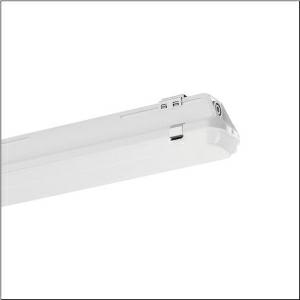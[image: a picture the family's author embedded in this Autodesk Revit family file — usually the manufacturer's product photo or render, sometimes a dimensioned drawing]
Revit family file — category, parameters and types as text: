
# Revit family: monsun_r__21_51fb207l440k005_b217
name_source: partatom
category: Lighting Fixtures
units: mm (PartAtom-declared; Revit-internal decimal feet)

## family parameters
Cut with Voids When Loaded = No
Host = Face
Light Source = No
Part Type = Normal
Room Calculation Point = No
Round Connector Dimension = Use Diameter
Shared = No

## types (1)
- Monsun® 21 (1 x LED, 4330 lm, 27.2 W, 4000K)
    Apparent Load = 27 VA
    CIE Flux Codes = 45 75 93 94 100
    Color Rendering = 80
    Color Temperature = 4000K
    Default Elevation = 1800 mm
    Description = Monsun® 21, damp-proof luminaire, chain hanger, primary optical cover: enclosure, of PC, light emission: direct distribution, primary light characteristic: symmetric, installation type: vertical mounting, horizontal mounting, surface-mounted, suspended mounting, LED, rated luminous flux: 4.330lm, luminous efficacy: 159lm/W, light colour: 840, colour temperature: 4000K, control gear: ON/OFF, with terminal, 3-pole, max. 2.5mm², through-wiring: 5x 2.5mm², mains connection: 220..240V, AC, 50/60Hz, rated input power: 27W, housing, of glass-fibre reinforced plastic, uncoated, bright grey, incl. chain hanger, length: 1.299mm, width: 90mm, height: 88mm, clip for enclosure, of stainless steel (V2A), ceiling mounting element, of stainless steel (V2A), chain hanger, of stainless steel (V2A), protection rating (complete): IP66, insulation class (complete): insulation class I (protective earthing), certification: CE, ENEC, VDE, UKCA, protection symbol: D, impact resistance: IK08, permissible operating ambient temperature: -25..+35°C, standard: EN 50419, EN 60598-2-1, corresponds to IFS (International Featured Standards) requirements for safety and quality in the food industry, for indoor or canopied outdoor use, no direct snow, no direct sun, no direct rain, LABS conformity tested according to VDMA 24364:2018-05, contact your sales advisor before using the luminaires in applications with unclear chemical exposure, large temperature fluctuations or condensation-forming humidity, packaging unit: 1 piece
    Height = 88 mm
    Lamp = 1 x LED
    Lamp Light Flux = 4330 lm
    Lamp Power = 27.2 W
    Lamp count = 1
    Length = 1299 mm
    Luminous efficacy = 159 lm/W
    Manufacturer = Siteco
    ModVariant = No
    Model = 51FB207L440K005
    Mounting Place = Ceiling
    Mounting Type = Surface mounted
    Number of Poles = 1
    OnlyDefault = Yes
    Power Factor = 1
    Product Name = Monsun® 21
    Product group = damp-proof luminaire
    ProductGroupID = 300
    Protection Class = Protection class I
    Protection Degree = IP 66
    RLX_Detail_Level = 1
    RLX_Emergency_Light_Flux = 0 lm
    RLX_Emergency_Type = 0
    RLX_Emergency_Type_DB = No
    RlxData = <blob elided: 89777 chars, md5=ddecc001>
    Socket = socket
    Standby Power = 0 W
    System Light Flux = 4330 lm
    System Power = 27 W
    Type Comments = Product without accessories
    Type Image = l_1319656.jpg
    URL = http://relux.com
    VarID = ---
    Voltage = 0 V
    Weight = 0.00 kg
    Width = 90 mm

## geometry (parser evidence)
native form markers: Blend x4, Sweep x14
no freeform markers — native parametric forms only
